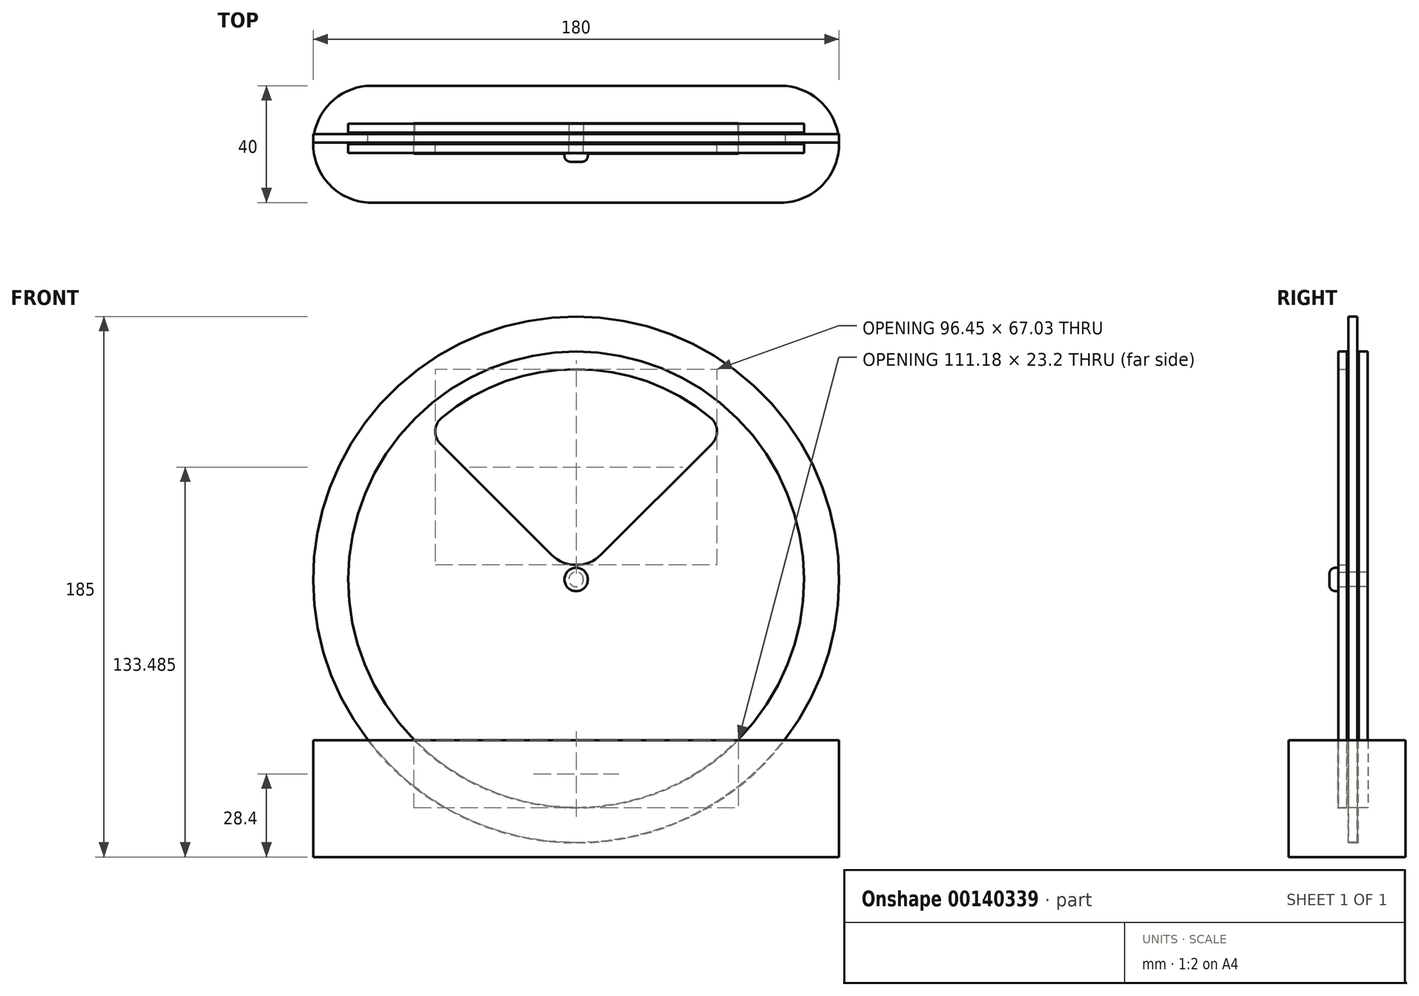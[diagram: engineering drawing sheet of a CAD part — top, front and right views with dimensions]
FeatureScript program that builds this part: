
annotation { "Feature Type Name" : "Feature", "Feature Type Description" : "" }
export const myFeature = defineFeature(function(context is Context, id is Id, definition is map)
    precondition{}
    {
        {
            assignVariable(context, id + "F0", {"name" : "thickness", "anyValue" : 3});
        }
        {
            var Q0;
            Q0=qCreatedBy(makeId("Top.planeOp"),FACE);
            var sketch = newSketch(context, id + "F1", { "sketchPlane" : qUnion([Q0])});
            skLineSegment(sketch, "E0.bottom", {"start": v(90, 20) * mm, "end": v(-90, 20) * mm});
            skLineSegment(sketch, "E0.top", {"start": v(90, -20) * mm, "end": v(-90, -20) * mm});
            skLineSegment(sketch, "E0.left", {"start": v(90, 20) * mm, "end": v(90, -20) * mm});
            skLineSegment(sketch, "E0.right", {"start": v(-90, 20) * mm, "end": v(-90, -20) * mm});
            skPoint(sketch, "E0.middle", {"position": v(0, 0) * mm});
            skArc(sketch, "E1", {"start": v(-70, 20) * mm, "mid": v(-90, 0) * mm, "end": v(-70, -20) * mm});
            skArc(sketch, "E2", {"start": v(70, -20) * mm, "mid": v(90, 0) * mm, "end": v(70, 20) * mm});
            skSolve(sketch);
        }
        {
            var Q0;
            {var subQ0=sQuery(id+"F1.wireOp",EDGE,"E1");var subQ4=sQuery(id+"F1.wireOp",EDGE,"E0.bottom");var subQ5=makeQuery(id+"F1.imprint","INTERSECT",VERTEX,{"derivedFrom":[subQ4,subQ0]});Q0=makeQuery(id+"F1.imprint","IMPRINT",FACE,{"disambiguationData":[TD([[makeQuery(id+"F1.imprint","IMPRINT",EDGE,{"disambiguationData":[TD([[subQ5,1.0]])],"derivedFrom":subQ4}),1.0]])]});}
            extrude(context, id + "F2", {"entities" : qUnion([Q0]), "depth" : 40 * mm});
        }
        {
            var Q0;
            Q0=qCreatedBy(makeId("Front.planeOp"),FACE);
            var sketch = newSketch(context, id + "F3", { "sketchPlane" : qUnion([Q0])});
            skCircle(sketch, "E3", {"center": v(0, 95) * mm, "radius": 90 * mm});
            skCircle(sketch, "E4.0", {"center": v(0, 95) * mm, "radius": 78 * mm});
            skLineSegment(sketch, "E5", {"start": v(0, 95) * mm, "end": v(0, 0) * mm, "construction": true});
            skLineSegment(sketch, "E6", {"start": v(-46.48, 141.48) * mm, "end": v(-8.49, 103.49) * mm});
            skLineSegment(sketch, "E7.MirrorCS", {"start": v(46.48, 141.48) * mm, "end": v(8.49, 103.49) * mm});
            skPoint(sketch, "E8.orphan", {"position": v(-63.64, 31.36) * mm});
            skPoint(sketch, "E9.orphan", {"position": v(63.64, 31.36) * mm});
            skArc(sketch, "E10", {"start": v(-46.07, 150.33) * mm, "mid": v(0, 167) * mm, "end": v(46.07, 150.33) * mm});
            skPoint(sketch, "E11.orphan", {"position": v(55.15, 150.15) * mm});
            skPoint(sketch, "E12.visualSharp", {"position": v(-50.91, 145.91) * mm});
            skArc(sketch, "E12.filletArc", {"start": v(-46.07, 150.33) * mm, "mid": v(-48.23, 146) * mm, "end": v(-46.48, 141.48) * mm});
            skPoint(sketch, "E13.visualSharp", {"position": v(50.91, 145.91) * mm});
            skArc(sketch, "E13.filletArc", {"start": v(46.48, 141.48) * mm, "mid": v(48.23, 146) * mm, "end": v(46.07, 150.33) * mm});
            skArc(sketch, "E14.filletArc", {"start": v(-8.49, 103.49) * mm, "mid": v(0, 99.97) * mm, "end": v(8.49, 103.49) * mm});
            skCircle(sketch, "E15", {"center": v(0, 95) * mm, "radius": 2.5 * mm});
            skLineSegment(sketch, "E16", {"start": v(-90, 0) * mm, "end": v(-90, 40) * mm, "construction": true});
            skSolve(sketch);
        }
        {
            var Q0;
            Q0=makeQuery(id+"F3.imprint","IMPRINT",FACE,{"disambiguationData":[TD([[makeQuery(id+"F3.imprint","IMPRINT",EDGE,{"derivedFrom":sQuery(id+"F3.wireOp",EDGE,"E4.0")}),1.0]])]});
            extrude(context, id + "F4", {"entities" : qUnion([Q0]), "depth" : (getVariable(context, 'thickness')) * mm});
        }
        {
            var Q0;
            Q0=makeQuery(id+"F3.imprint","IMPRINT",FACE,{"disambiguationData":[TD([[makeQuery(id+"F3.imprint","IMPRINT",EDGE,{"derivedFrom":sQuery(id+"F3.wireOp",EDGE,"E3")}),1.0]])]});
            var Q1;
            Q1=makeQuery(id+"F3.imprint","IMPRINT",FACE,{"disambiguationData":[TD([[makeQuery(id+"F3.imprint","IMPRINT",EDGE,{"derivedFrom":sQuery(id+"F3.wireOp",EDGE,"E4.0")}),1.0]])]});
            var Q2;
            Q2=makeQuery(id+"F3.imprint","IMPRINT",FACE,{"disambiguationData":[TD([[makeQuery(id+"F3.imprint","IMPRINT",EDGE,{"derivedFrom":sQuery(id+"F3.wireOp",EDGE,"E6")}),1.0]])]});
            extrude(context, id + "F5", {"entities" : qUnion([Q0, Q1, Q2]), "oppositeDirection" : true, "depth" : (0.5 + getVariable(context, 'thickness')) * mm, "hasSecondDirection" : true, "secondDirectionOppositeDirection" : true, "secondDirectionDepth" : 0.5 * mm});
        }
        {
            var Q0;
            Q0=makeQuery(id+"F3.imprint","IMPRINT",FACE,{"disambiguationData":[TD([[makeQuery(id+"F3.imprint","IMPRINT",EDGE,{"derivedFrom":sQuery(id+"F3.wireOp",EDGE,"E4.0")}),1.0]])]});
            var Q1;
            Q1=makeQuery(id+"F3.imprint","IMPRINT",FACE,{"disambiguationData":[TD([[makeQuery(id+"F3.imprint","IMPRINT",EDGE,{"derivedFrom":sQuery(id+"F3.wireOp",EDGE,"E6")}),1.0]])]});
            extrude(context, id + "F6", {"entities" : qUnion([Q0, Q1]), "oppositeDirection" : true, "depth" : (4 + getVariable(context, 'thickness')) * mm, "hasSecondDirection" : true, "secondDirectionOppositeDirection" : true, "secondDirectionDepth" : 4 * mm});
        }
        {
            var Q0;
            Q0=makeQuery(id+"F6.opExtrude","SWEPT_BODY",BODY,{"disambiguationData":[OSD([sQuery(id+"F3.wireOp",EDGE,"E4.0"),sQuery(id+"F3.wireOp",EDGE,"E15")])]});
            var Q1;
            Q1=makeQuery(id+"F5.opExtrude","SWEPT_BODY",BODY,{"disambiguationData":[OSD([sQuery(id+"F3.wireOp",EDGE,"E3"),sQuery(id+"F3.wireOp",EDGE,"E15")])]});
            var Q2;
            Q2=makeQuery(id+"F4.opExtrude","SWEPT_BODY",BODY,{"disambiguationData":[OSD([sQuery(id+"F3.wireOp",EDGE,"E4.0"),sQuery(id+"F3.wireOp",EDGE,"E6"),sQuery(id+"F3.wireOp",EDGE,"E7.MirrorCS"),sQuery(id+"F3.wireOp",EDGE,"E10"),sQuery(id+"F3.wireOp",EDGE,"E12.filletArc"),sQuery(id+"F3.wireOp",EDGE,"E13.filletArc"),sQuery(id+"F3.wireOp",EDGE,"E14.filletArc"),sQuery(id+"F3.wireOp",EDGE,"E15")])]});
            var Q3;
            Q3=makeQuery(id+"F2.opExtrude","SWEPT_BODY",BODY,{"disambiguationData":[OSD([sQuery(id+"F1.wireOp",EDGE,"E0.bottom"),sQuery(id+"F1.wireOp",EDGE,"E0.top"),sQuery(id+"F1.wireOp",EDGE,"E0.left"),sQuery(id+"F1.wireOp",EDGE,"E0.right")])]});
            booleanBodies(context, id + "F7", {"operationType" : BooleanOperationType.SUBTRACTION, "tools" : qUnion([Q0, Q1, Q2]), "targets" : qUnion([Q3]), "offset" : true, "offsetAll" : true, "offsetDistance" : 0.2 * mm, "keepTools" : true});
        }
        {
            var Q0;
            Q0=makeQuery(id+"F4.opExtrude","CAP_FACE",FACE,{"disambiguationData":[OSD([sQuery(id+"F3.wireOp",EDGE,"E4.0"),sQuery(id+"F3.wireOp",EDGE,"E6"),sQuery(id+"F3.wireOp",EDGE,"E7.MirrorCS"),sQuery(id+"F3.wireOp",EDGE,"E10"),sQuery(id+"F3.wireOp",EDGE,"E12.filletArc"),sQuery(id+"F3.wireOp",EDGE,"E13.filletArc"),sQuery(id+"F3.wireOp",EDGE,"E14.filletArc"),sQuery(id+"F3.wireOp",EDGE,"E15")])],"isStart":false});
            var sketch = newSketch(context, id + "F8", { "sketchPlane" : qUnion([Q0])});
            skCircle(sketch, "E17", {"center": v(0, 95) * mm, "radius": 4 * mm});
            skSolve(sketch);
        }
        {
            var Q0;
            Q0=makeQuery(id+"F8.imprint","IMPRINT",FACE,{"disambiguationData":[TD([[makeQuery(id+"F8.imprint","IMPRINT",EDGE,{"derivedFrom":sQuery(id+"F8.wireOp",EDGE,"E17")}),1.0]])]});
            var Q1;
            Q1=makeQuery(id+"F8.imprint","IMPRINT",FACE,{"disambiguationData":[TD([[makeQuery(id+"F8.imprint","IMPRINT",EDGE,{"derivedFrom":makeQuery(id+"F4.opExtrude","CAP_EDGE",EDGE,{"disambiguationData":[OSD([sQuery(id+"F3.wireOp",EDGE,"E15")])],"isStart":false})}),1.0]])]});
            extrude(context, id + "F9", {"entities" : qUnion([Q0, Q1]), "depth" : 3 * mm});
        }
        {
            var Q0;
            Q0=makeQuery(id+"F9.opExtrude","CAP_EDGE",EDGE,{"disambiguationData":[OSD([sQuery(id+"F8.wireOp",EDGE,"E17")])],"isStart":false});
            fillet(context, id + "F10", {"entities" : qUnion([Q0]), "radius" : 2 * mm, "tangentPropagation" : true, "allowEdgeOverflow" : false});
        }
        {
            var Q0;
            Q0=makeQuery(id+"F7.tempBoolean.opBoolean","COPY",FACE,{"derivedFrom":makeQuery(id+"F7.offsetTempBody.opPattern","COPY",FACE,{"derivedFrom":makeQuery(id+"F4.opExtrude","CAP_FACE",FACE,{"disambiguationData":[OSD([sQuery(id+"F3.wireOp",EDGE,"E4.0"),sQuery(id+"F3.wireOp",EDGE,"E6"),sQuery(id+"F3.wireOp",EDGE,"E7.MirrorCS"),sQuery(id+"F3.wireOp",EDGE,"E10"),sQuery(id+"F3.wireOp",EDGE,"E12.filletArc"),sQuery(id+"F3.wireOp",EDGE,"E13.filletArc"),sQuery(id+"F3.wireOp",EDGE,"E14.filletArc"),sQuery(id+"F3.wireOp",EDGE,"E15")])],"isStart":true}),"instanceName":"1"})});
            var Q1;
            Q1=makeQuery(id+"F7.tempBoolean.opBoolean","COPY",FACE,{"derivedFrom":makeQuery(id+"F7.offsetTempBody.opPattern","COPY",FACE,{"derivedFrom":makeQuery(id+"F6.opExtrude","CAP_FACE",FACE,{"disambiguationData":[OSD([sQuery(id+"F3.wireOp",EDGE,"E4.0"),sQuery(id+"F3.wireOp",EDGE,"E15")])],"isStart":false}),"instanceName":"1"})});
            extrude(context, id + "F11", {"entities" : qUnion([Q0]), "operationType" : NewBodyOperationType.REMOVE, "endBound" : BoundingType.UP_TO_SURFACE, "oppositeDirection" : true, "endBoundEntityFace" : qUnion([Q1]), "depth" : 25 * mm});
        }
    });
